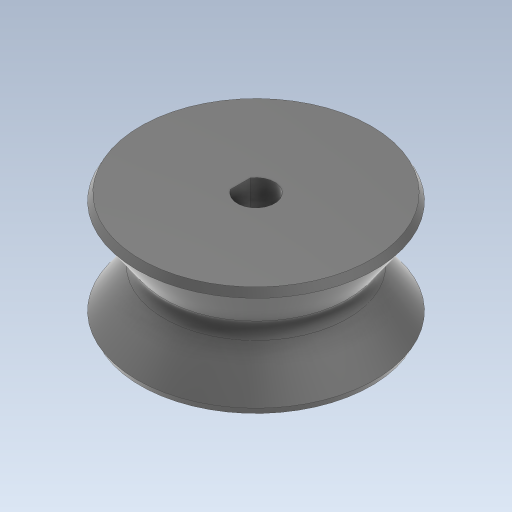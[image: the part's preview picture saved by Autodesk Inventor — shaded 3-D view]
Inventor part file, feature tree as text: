
AUTODESK INVENTOR PART (.ipt)
format: ipt  version: 2023 (Build 270158000, 158)  size: 197,120 bytes
history: native  units: mm
features: chamfer x3, plane x2, sketch x1, revolve x1, extrude x1, fillet x1, hole x1
ambient origin geometry x8: Origin, YZ Plane, XZ Plane, XY Plane, X Axis, Y Axis, Z Axis, Center Point
bodies: Solid1 (feature_tree)
feature tree (10):
  sketch  "Sketch1"  dims[d1=4.7mm d4=15.0mm d5=14.0mm d6=14.0mm d7=90.0deg d8=0.0mm d9=0.0mm d10=1.2mm d11=2.0mm d12=45.0deg d15=30.0deg d20=3.490659mm d71=-12.0mm d92=2.55mm d93=10.0mm d95=2.0mm d98=1.0mm d99=2.0mm d100=45.0deg d102=9.599311mm d103=10.0mm d105=6.5mm d106=6.0mm d107=6.0mm d108=2.0mm d109=90.0deg d110=5.3mm d111=0.0mm d112=0.2mm d113=2.0mm d114=45.0deg]
  revolve  "Revolution1"  [1 undecoded]
  extrude  "Extrusion1"  Depth=5.3mm
  chamfer  "Chamfer1"  Distance=14.0mm
  plane  "Work Plane3"
  plane  "Work Plane4"
  fillet  "Fillet1"  [1 undecoded]
  chamfer  "Chamfer2"  [1 undecoded]
  hole  "Hole4"  [1 undecoded]
  chamfer  "Chamfer3"  Distance=3.490659mm Angle=30.0deg
note: 4 required parameter values undecoded (feature->parameter linkage not recoverable at this tier; creation-order binding heuristic only, values carry confidence <= 0.55)